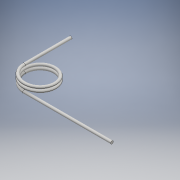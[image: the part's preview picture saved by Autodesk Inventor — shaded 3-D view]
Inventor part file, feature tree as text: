
AUTODESK INVENTOR PART (.ipt)
format: ipt  version: 2016 (Build 200138000, 138)  size: 162,816 bytes
history: native  units: mm
features: sketch x4, helix x2, extrude x2
ambient origin geometry x8: Origin, YZ Plane, XZ Plane, XY Plane, X Axis, Y Axis, Z Axis, Center Point
bodies: Solid1 (feature_tree)
feature tree (8):
  helix  "Coil1"  [1 undecoded]
  extrude  "Extrusion1"  Depth=17.0mm TaperAngle=0.0deg
  helix  "Coil2"  [1 undecoded]
  extrude  "Extrusion2"  [1 undecoded]
  sketch  "Sketch1"  dims[d3=1.0mm]
  sketch  "Sketch2"  dims[d4=0.1mm d5=2.5mm d6=20.0mm d7=0.0mm d8=90.0deg d9=90.0deg d10=0.0mm d11=0.0mm d12=17.0mm d13=0.0mm]
  sketch  "Sketch3"  dims[d14=0.1mm d15=0.5mm d16=2.5mm d17=0.0mm d18=90.0deg d19=90.0deg d20=0.0mm d21=0.0mm d22=32.0mm d23=0.0mm]
  sketch  "Sketch4"
note: 3 required parameter values undecoded (feature->parameter linkage not recoverable at this tier; creation-order binding heuristic only, values carry confidence <= 0.55)
